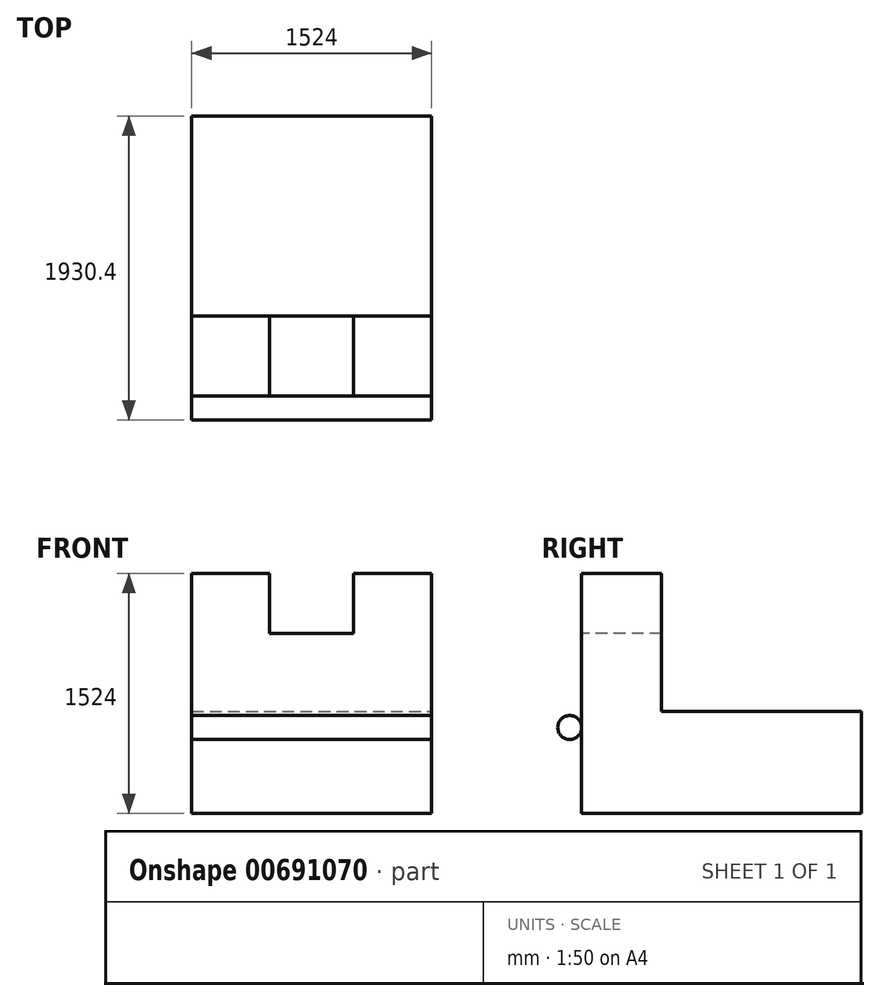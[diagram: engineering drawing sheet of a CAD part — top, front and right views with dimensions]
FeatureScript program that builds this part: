
annotation { "Feature Type Name" : "Feature", "Feature Type Description" : "" }
export const myFeature = defineFeature(function(context is Context, id is Id, definition is map)
    precondition{}
    {
        {
            var Q0;
            Q0=qCreatedBy(makeId("Front.planeOp"),FACE);
            var sketch = newSketch(context, id + "F0", { "sketchPlane" : qUnion([Q0])});
            skLineSegment(sketch, "E0.bottom", {"start": v(762, 762) * mm, "end": v(-762, 762) * mm});
            skLineSegment(sketch, "E0.top", {"start": v(762, -762) * mm, "end": v(-762, -762) * mm});
            skLineSegment(sketch, "E0.left", {"start": v(762, 762) * mm, "end": v(762, -762) * mm});
            skLineSegment(sketch, "E0.right", {"start": v(-762, 762) * mm, "end": v(-762, -762) * mm});
            skPoint(sketch, "E0.middle", {"position": v(0, 0) * mm});
            skSolve(sketch);
        }
        {
            var Q0;
            Q0=makeQuery(id+"F0.imprint","IMPRINT",FACE,{"disambiguationData":[TD([[makeQuery(id+"F0.imprint","IMPRINT",EDGE,{"derivedFrom":sQuery(id+"F0.wireOp",EDGE,"E0.bottom")}),1.0]])]});
            extrude(context, id + "F1", {"entities" : qUnion([Q0]), "depth" : 508 * mm, "offsetDistance" : 25.4 * mm});
        }
        {
            var Q0;
            Q0=makeQuery(id+"F1.opExtrude","CAP_FACE",FACE,{"disambiguationData":[OSD([sQuery(id+"F0.wireOp",EDGE,"E0.bottom"),sQuery(id+"F0.wireOp",EDGE,"E0.top"),sQuery(id+"F0.wireOp",EDGE,"E0.left"),sQuery(id+"F0.wireOp",EDGE,"E0.right")])],"isStart":false});
            var sketch = newSketch(context, id + "F2", { "sketchPlane" : qUnion([Q0])});
            skLineSegment(sketch, "E1.bottom", {"start": v(-266.7, 762) * mm, "end": v(266.7, 762) * mm});
            skLineSegment(sketch, "E1.top", {"start": v(-266.7, 381) * mm, "end": v(266.7, 381) * mm});
            skLineSegment(sketch, "E1.left", {"start": v(-266.7, 762) * mm, "end": v(-266.7, 381) * mm});
            skLineSegment(sketch, "E1.right", {"start": v(266.7, 762) * mm, "end": v(266.7, 381) * mm});
            skLineSegment(sketch, "E2", {"start": v(0, 381) * mm, "end": v(0, 0) * mm, "construction": true});
            skSolve(sketch);
        }
        {
            var Q0;
            Q0=makeQuery(id+"F2.imprint","IMPRINT",FACE,{"disambiguationData":[TD([[makeQuery(id+"F2.imprint","IMPRINT",EDGE,{"derivedFrom":sQuery(id+"F2.wireOp",EDGE,"E1.bottom")}),1.0]])]});
            extrude(context, id + "F3", {"entities" : qUnion([Q0]), "operationType" : NewBodyOperationType.REMOVE, "endBound" : BoundingType.THROUGH_ALL, "oppositeDirection" : true, "depth" : 25.4 * mm, "offsetDistance" : 25.4 * mm});
        }
        {
            var Q0;
            Q0=makeQuery(id+"F1.opExtrude","SWEPT_FACE",FACE,{"disambiguationData":[OSD([sQuery(id+"F0.wireOp",EDGE,"E0.left")])]});
            var sketch = newSketch(context, id + "F4", { "sketchPlane" : qUnion([Q0])});
            skLineSegment(sketch, "E3.bottom", {"start": v(0, -114.3) * mm, "end": v(1270, -114.3) * mm});
            skLineSegment(sketch, "E3.top", {"start": v(0, -762) * mm, "end": v(1270, -762) * mm});
            skLineSegment(sketch, "E3.left", {"start": v(0, -114.3) * mm, "end": v(0, -762) * mm});
            skLineSegment(sketch, "E3.right", {"start": v(1270, -114.3) * mm, "end": v(1270, -762) * mm});
            skSolve(sketch);
        }
        {
            var Q0;
            Q0=makeQuery(id+"F4.imprint","IMPRINT",FACE,{"disambiguationData":[TD([[makeQuery(id+"F4.imprint","IMPRINT",EDGE,{"derivedFrom":sQuery(id+"F4.wireOp",EDGE,"E3.bottom")}),-1.0]])]});
            var Q1;
            Q1=makeQuery(id+"F1.opExtrude","SWEPT_FACE",FACE,{"disambiguationData":[OSD([sQuery(id+"F0.wireOp",EDGE,"E0.right")])]});
            extrude(context, id + "F5", {"entities" : qUnion([Q0]), "operationType" : NewBodyOperationType.ADD, "endBound" : BoundingType.UP_TO_SURFACE, "oppositeDirection" : true, "depth" : 25.4 * mm, "endBoundEntityFace" : qUnion([Q1]), "offsetDistance" : 25.4 * mm});
        }
        {
            var Q0;
            {var subQ3=sQuery(id+"F4.wireOp",EDGE,"E3.left");Q0=makeQuery(id+"F4.imprint","IMPRINT",FACE,{"disambiguationData":[TD([[makeQuery(id+"F4.imprint","IMPRINT",EDGE,{"derivedFrom":subQ3}),-1.0]])]});}
            var sketch = newSketch(context, id + "F6", { "sketchPlane" : qUnion([Q0])});
            skCircle(sketch, "E4", {"center": v(-584.2, -215.9) * mm, "radius": 76.2 * mm});
            skSolve(sketch);
        }
        {
            var Q0;
            Q0=makeQuery(id+"F6.imprint","IMPRINT",FACE,{"disambiguationData":[TD([[makeQuery(id+"F6.imprint","IMPRINT",EDGE,{"derivedFrom":sQuery(id+"F6.wireOp",EDGE,"E4")}),1.0]])]});
            var Q1;
            Q1=makeQuery(id+"F5.boolean.opBoolean","MERGE",FACE,{"derivedFrom":[makeQuery(id+"F1.opExtrude","SWEPT_FACE",FACE,{"disambiguationData":[OSD([sQuery(id+"F0.wireOp",EDGE,"E0.right")])]}),makeQuery(id+"F5.opExtrude","CAP_FACE",FACE,{"disambiguationData":[OSD([sQuery(id+"F4.wireOp",EDGE,"E3.bottom"),sQuery(id+"F4.wireOp",EDGE,"E3.top"),sQuery(id+"F4.wireOp",EDGE,"E3.left"),sQuery(id+"F4.wireOp",EDGE,"E3.right")])],"isStart":false})]});
            extrude(context, id + "F7", {"entities" : qUnion([Q0]), "operationType" : NewBodyOperationType.ADD, "endBound" : BoundingType.UP_TO_SURFACE, "oppositeDirection" : true, "depth" : 25.4 * mm, "endBoundEntityFace" : qUnion([Q1]), "offsetDistance" : 25.4 * mm});
        }
    });
